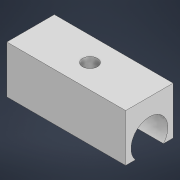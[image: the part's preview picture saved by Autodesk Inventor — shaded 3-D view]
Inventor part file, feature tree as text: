
AUTODESK INVENTOR PART (.ipt)
format: ipt  version: 2022 (Build 260153000, 153)  size: 107,008 bytes
history: native  units: mm
features: extrude x3, sketch x3
ambient origin geometry x8: Origin, YZ Plane, XZ Plane, XY Plane, X Axis, Y Axis, Z Axis, Center Point
bodies: Solid1 (feature_tree)
feature tree (6):
  extrude  "Extrusion1"  Depth=8.0mm
  extrude  "Extrusion2"  Depth=8.0mm
  extrude  "Extrusion3"  Depth=20.0mm TaperAngle=0.0deg
  sketch  "Sketch1"  dims[d0=20.0mm d1=8.0mm]
  sketch  "Sketch2"  dims[d2=8.0mm d3=0.0mm d4=2.0mm]
  sketch  "Sketch3"  dims[d5=6.2mm d6=20.0mm d7=0.0mm d8=2.5mm d9=2.5mm d10=0.0mm]
